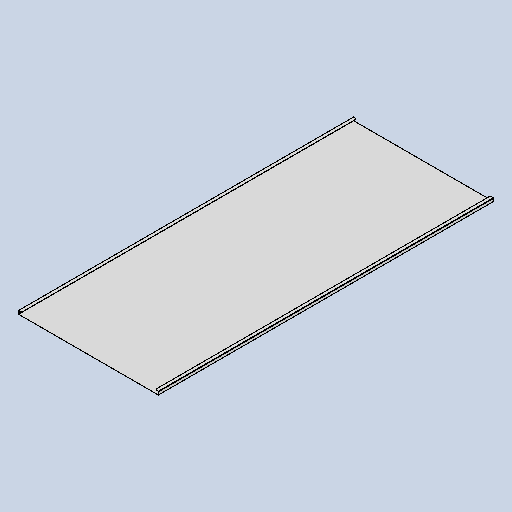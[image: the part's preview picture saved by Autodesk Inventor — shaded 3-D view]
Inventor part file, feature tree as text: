
AUTODESK INVENTOR PART (.ipt)
format: ipt  version: 2025 (Build 290162010, 162A)  size: 201,728 bytes
history: native  units: mm
features: sheet_metal_op x13, other x6, sketch x5, chamfer x1
ambient origin geometry x8: Origin, YZ Plane, XZ Plane, XY Plane, X Axis, Y Axis, Z Axis, Center Point
bodies: Body1 (feature_tree)
feature tree (25):
  sheet_metal_op  "Face1"
  sheet_metal_op  "Flange2"
  sheet_metal_op  "Flange3"
  sheet_metal_op  "Flange4"
  sheet_metal_op  "Flange5"
  chamfer  "Corner Round1"
  sketch  "Sketch6"  dims[d12=23.212879mm]
  other  "Plate2"
  sketch  "Sketch11"  dims[d52=411.0mm]
  other  "Plate4"
  sheet_metal_op  "Bend3"
  sheet_metal_op  "Corner3"
  sketch  "Sketch12"  dims[d53=980.0mm]
  other  "Plate5"
  sheet_metal_op  "Bend4"
  sheet_metal_op  "Corner4"
  sketch  "Sketch13"  dims[d54=0.5mm]
  other  "Plate6"
  sheet_metal_op  "Bend5"
  sheet_metal_op  "Corner5"
  sketch  "Sketch14"  dims[d84=0.5mm d85=0.25mm d86=1.0mm d87=0.5mm d88=10.0mm d89=90.0deg d90=0.5mm d91=2.0mm d92=0.5mm d93=0.5mm d94=0.5mm d95=0.25mm d96=1.0mm d97=0.5mm d98=10.0mm d99=90.0deg d100=0.5mm d101=2.0mm d102=0.5mm d103=0.5mm d104=0.5mm d105=0.25mm d106=1.0mm d107=0.5mm d108=10.0mm d109=90.0deg d110=0.5mm d111=2.0mm d112=0.5mm d113=0.5mm d114=0.5mm d115=0.25mm d116=1.0mm d117=0.5mm d118=10.0mm d119=90.0deg d120=0.5mm d121=2.0mm d122=0.5mm d123=0.5mm d124=4.0mm]
  other  "Plate7"
  sheet_metal_op  "Bend6"
  sheet_metal_op  "Corner6"
  other  "Definition1"
